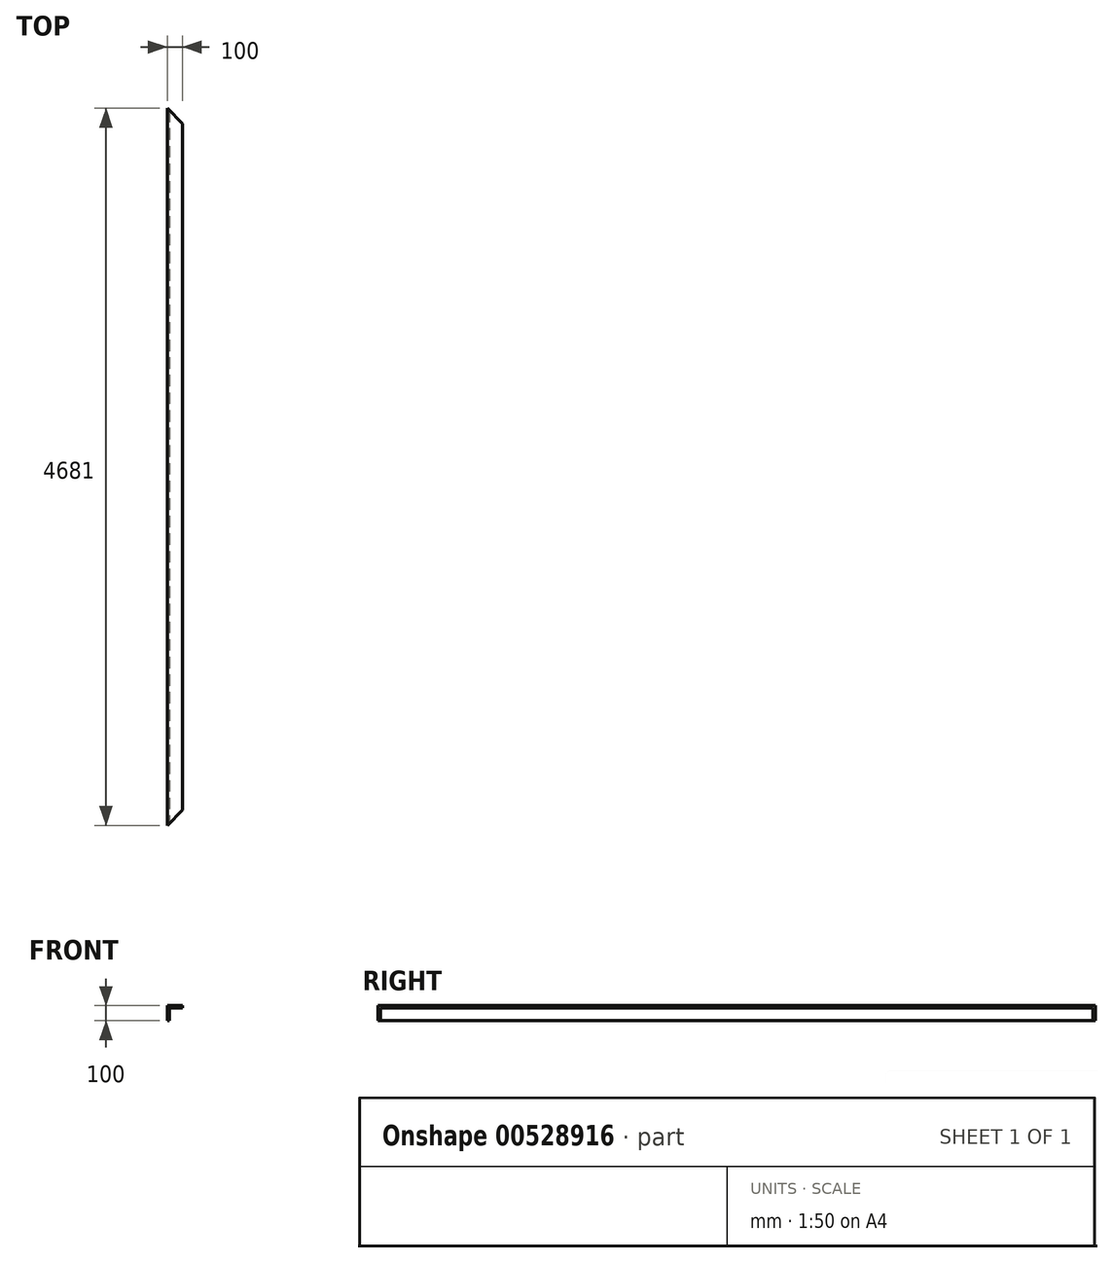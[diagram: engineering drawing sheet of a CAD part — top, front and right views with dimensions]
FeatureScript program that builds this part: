
annotation { "Feature Type Name" : "Feature", "Feature Type Description" : "" }
export const myFeature = defineFeature(function(context is Context, id is Id, definition is map)
    precondition{}
    {
        {
            var Q0;
            Q0=qCreatedBy(makeId("Top.planeOp"),FACE);
            var sketch = newSketch(context, id + "F0", { "sketchPlane" : qUnion([Q0])});
            skLineSegment(sketch, "E0", {"start": v(0, -2340.5) * mm, "end": v(0, 2340.5) * mm});
            skLineSegment(sketch, "E1", {"start": v(-100, -2240.5) * mm, "end": v(-100, 2240.5) * mm});
            skLineSegment(sketch, "E2", {"start": v(0, -2340.5) * mm, "end": v(-100, -2240.5) * mm});
            skLineSegment(sketch, "E3", {"start": v(0, 2340.5) * mm, "end": v(-100, 2240.5) * mm});
            skSolve(sketch);
        }
        {
            var Q0;
            Q0=makeQuery(id+"F0.imprint","IMPRINT",FACE,{"disambiguationData":[TD([[makeQuery(id+"F0.imprint","IMPRINT",EDGE,{"derivedFrom":sQuery(id+"F0.wireOp",EDGE,"E0")}),1.0]])]});
            extrude(context, id + "F1", {"entities" : qUnion([Q0]), "depth" : 15 * mm, "offsetDistance" : 25 * mm});
        }
        {
            var Q0;
            Q0=makeQuery(id+"F1.opExtrude","CAP_FACE",FACE,{"disambiguationData":[OSD([sQuery(id+"F0.wireOp",EDGE,"E0"),sQuery(id+"F0.wireOp",EDGE,"E1"),sQuery(id+"F0.wireOp",EDGE,"E2"),sQuery(id+"F0.wireOp",EDGE,"E3")])],"isStart":false});
            var sketch = newSketch(context, id + "F2", { "sketchPlane" : qUnion([Q0])});
            skLineSegment(sketch, "E4.0", {"start": v(0, -2340.5) * mm, "end": v(0, 2340.5) * mm});
            skLineSegment(sketch, "E5", {"start": v(-15, 2325.5) * mm, "end": v(-15, -2325.5) * mm});
            skLineSegment(sketch, "E6", {"start": v(0, 2340.5) * mm, "end": v(-15, 2325.5) * mm});
            skLineSegment(sketch, "E7", {"start": v(-15, -2325.5) * mm, "end": v(0, -2340.5) * mm});
            skSolve(sketch);
        }
        {
            var Q0;
            Q0=makeQuery(id+"F2.imprint","IMPRINT",FACE,{"disambiguationData":[TD([[makeQuery(id+"F2.imprint","IMPRINT",EDGE,{"derivedFrom":sQuery(id+"F2.wireOp",EDGE,"E4.0")}),1.0]])]});
            extrude(context, id + "F3", {"entities" : qUnion([Q0]), "operationType" : NewBodyOperationType.ADD, "depth" : (100 - 15) * mm, "offsetDistance" : 25 * mm});
        }
        {
            var Q0;
            Q0=makeQuery(id+"F1.opExtrude","SWEPT_BODY",BODY,{"disambiguationData":[OSD([sQuery(id+"F0.wireOp",EDGE,"E0"),sQuery(id+"F0.wireOp",EDGE,"E1"),sQuery(id+"F0.wireOp",EDGE,"E2"),sQuery(id+"F0.wireOp",EDGE,"E3")])]});
            var Q1;
            Q1=qCreatedBy(makeId("Top.planeOp"),FACE);
            mirror(context, id + "F4", {"entities" : qUnion([Q0]), "mirrorPlane" : qUnion([Q1])});
        }
        {
            var Q0;
            Q0=makeQuery(id+"F1.opExtrude","SWEPT_BODY",BODY,{"disambiguationData":[OSD([sQuery(id+"F0.wireOp",EDGE,"E0"),sQuery(id+"F0.wireOp",EDGE,"E1"),sQuery(id+"F0.wireOp",EDGE,"E2"),sQuery(id+"F0.wireOp",EDGE,"E3")])]});
            deleteBodies(context, id + "F5", {"entities" : qUnion([Q0])});
        }
        {
            var Q0;
            Q0=makeQuery(id+"F4.opPattern","COPY",BODY,{"derivedFrom":makeQuery(id+"F1.opExtrude","SWEPT_BODY",BODY,{"disambiguationData":[OSD([sQuery(id+"F0.wireOp",EDGE,"E0"),sQuery(id+"F0.wireOp",EDGE,"E1"),sQuery(id+"F0.wireOp",EDGE,"E2"),sQuery(id+"F0.wireOp",EDGE,"E3")])]}),"instanceName":"1"});
            var Q1;
            Q1=qCreatedBy(makeId("Right.planeOp"),FACE);
            mirror(context, id + "F6", {"entities" : qUnion([Q0]), "mirrorPlane" : qUnion([Q1])});
        }
        {
            var Q0;
            Q0=makeQuery(id+"F4.opPattern","COPY",BODY,{"derivedFrom":makeQuery(id+"F1.opExtrude","SWEPT_BODY",BODY,{"disambiguationData":[OSD([sQuery(id+"F0.wireOp",EDGE,"E0"),sQuery(id+"F0.wireOp",EDGE,"E1"),sQuery(id+"F0.wireOp",EDGE,"E2"),sQuery(id+"F0.wireOp",EDGE,"E3")])]}),"instanceName":"1"});
            deleteBodies(context, id + "F7", {"entities" : qUnion([Q0])});
        }
    });
